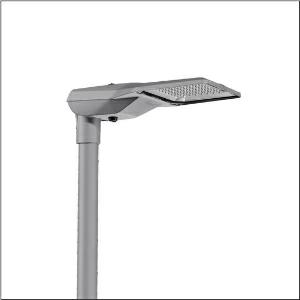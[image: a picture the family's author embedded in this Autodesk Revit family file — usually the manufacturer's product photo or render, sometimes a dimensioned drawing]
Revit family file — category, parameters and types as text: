
# Revit family: streetlight_sl_21_midi___pl52_5xe3h33t08mb_7712
name_source: partatom
category: Lighting Fixtures
units: mm (PartAtom-declared; Revit-internal decimal feet)

## family parameters
Cut with Voids When Loaded = No
Host = Face
Light Source = No
Part Type = Normal
Room Calculation Point = No
Round Connector Dimension = Use Diameter
Shared = No

## types (1)
- --- (1 x LED, 17960 lm, 136 W, 3000K)
    Apparent Load = 136 VA
    CIE Flux Codes = 27 59 98 100 100
    Color Rendering = 70
    Color Temperature = 3000K
    Default Elevation = 1800 mm
    Description = Streetlight SL 21 midi, mast luminaire, primary light control with lens, of PMMA, primary optical cover: cover, of toughened safety glass, transparent, light distribution: PL52, light emission: direct distribution, primary light characteristic: asymmetric, installation type: side-entry, post-top, LED, High Power LED, rated luminous flux: 17.960lm, luminous efficacy: 132lm/W, light colour: 730, colour temperature: 3000K, control: overheat protection, constant luminous flux control, time-dependent luminous flux control, flexible luminous flux parameterisation, presetting dimming logarithmic, mains connection: 230..240V, AC, 50/60Hz, start of lifetime: 136W, end of service life: 142W, reduction: 61W, luminaire housing, of diecast aluminium, powder-coated, Siteco® metallic grey (DB 702S), corrosivity category C5 mid according to DIN EN ISO 12944, please order mast flange separately, inclination adjustable: 0°, 5°, 10°, 15°, sealing non-destructively replaceable, multi-level sealing system, length: 644mm, width: 335mm, height: 110mm, mast flange for spigot size: 42mm (side-entry): 5XC10008XM4, 60/48mm (side-entry/post-top): 5XC10108XM2, 76/60mm (side-entry/post-top): 5XC10108XM1, Smart Interface below and above, protection rating (complete): IP66, insulation class (complete): insulation class II (safety insulation), certification: CE, ENEC, ENEC+, VDE, impact resistance: IK09, permissible operating ambient temperature for outdoor applications: -40..+50°C, standard-compliant lighting for roads and squares, packaging unit: 1 piece

Light Distribution: PL52
    Height = 111 mm
    Lamp = 1 x LED
    Lamp Light Flux = 17960 lm
    Lamp Power = 136 W
    Lamp count = 1
    Length = 644 mm
    Luminous efficacy = 132 lm/W
    Manufacturer = Siteco
    ModVariant = No
    Model = 5XE3H33T08MB
    Number of Poles = 1
    OnlyDefault = Yes
    Power Factor = 1
    Product Name = Streetlight SL 21 midi | PL52
    Product group = mast luminaire | pylon top
    ProductGroupID = 6100
    Protection Class = Protection class II
    Protection Degree = IP 66
    RLX_Detail_Level = 1
    RLX_Emergency_Light_Flux = 0 lm
    RLX_Emergency_Type = 0
    RLX_Emergency_Type_DB = No
    RlxData = <blob elided: 100529 chars, md5=3f2a685d>
    Socket = socket
    Standby Power = 0 W
    System Light Flux = 17960 lm
    System Power = 136 W
    Type Comments = factory setting: luminous flux: 100 % | dim-lin: 254 | 695 mA
    Type Image = l_1004304.jpg
    URL = http://relux.com
    VarID = @adj_142913
    Voltage = 0 V
    Weight = 0.00 kg
    Width = 336 mm

## geometry (parser evidence)
native form markers: Blend x4, Sweep x9
no freeform markers — native parametric forms only
